# Revit family: Касетный компактный блок VRF системы
name_source: partatom
category: Mechanical Equipment
revit_build: Autodesk Revit 2016 (Build: 20150506_1715(x64)
units: mm (PartAtom-declared; Revit-internal decimal feet)

## family parameters
Cut with Voids When Loaded = No
Host = Face
Part Type = Normal
Room Calculation Point = No
Round Connector Dimension = Use Diameter
Shared = No

## types (5) — shared parameters
Default Elevation = 1219.2 mm  [stored 4 ft]
Артикул планка = 1022724
Вес = 20.00 kg
Вес декоративной планки = 2.40 kg
Высота = 270 mm  [stored 0.885827 ft]
Высота планки = 30 mm  [stored 0.0984252 ft]
Глубина = 570 mm  [stored 1.87008 ft]
Глубина планки = 650 mm  [stored 2.13255 ft]
Диаметр дренажного шлага = 25 mm  [stored 0.082021 ft]
Диаметр жидкостной трубы = 6.35 mm  [stored 0.0208333 ft]
Модель декоративной планки = ESVMCP-SF-600
Наименование = Касетный компактный блок VRF-системы
Наименование декоративной планки = Декоративная панель для кассетного компактного блока
Напор дренажной помпы, мм водяного столба = 650
Номинал предохранителя = 10 A
Производитель = Electrolux
Таблица модель = Модель
Таблица модель планка = Модель планка
Таблица наименование = Наименование
Таблица наименование планка = Наименование планка
Таблица напор дренажной помпы = Напор дренажной помпы
Таблица параметров = Таблица параметров
Таблица параметров планка = Таблица параметров планка
Таблица расход воздуха = Расход воздуха
Таблица тип хладагента = Тип хладагента
Таблица уровень звукового давления = Уровень звукового давления
Таблица электропитание = Электропитание
Фаза = 1
Частота сети = 50 Hz
Ширина = 570 mm  [stored 1.87008 ft]
Ширина планки = 650 mm  [stored 2.13255 ft]
Эл. питание(коннектор) = 220 V
Электропитание, (В) = 220

## per-type parameters (varying)
| type | Артикул | Диаметр газовой трубы | Максимальная потребляемая мощность | Расход воздуха, (м.куб/ч) | Теплопроизводительность | Уровень звукового давления, (Дб(А)) | Холодопроизводительность |
| ESVMC4/C-SF-22 | 1022680 | 12.7 mm  [stored 0.0416667 ft] | 0.12 kW | 570-540-384 | 2.80 kW | 32-30-28 | 2.20 kW |
| ESVMC4/C-SF-28 | 1022681 | 12.7 mm  [stored 0.0416667 ft] | 0.12 kW | 570-540-384 | 3.30 kW | 32-30-28 | 2.80 kW |
| ESVMC4/C-SF-36 | 1022682 | 12.7 mm  [stored 0.0416667 ft] | 0.12 kW | 570-540-384 | 4.20 kW | 32-30-28 | 3.60 kW |
| ESVMC4/C-SF-45 | 1022683 | 12.7 mm  [stored 0.0416667 ft] | 0.13 kW | 654-564-456 | 4.90 kW | 34-32-30 | 4.30 kW |
| ESVMC4/C-SF-50 | 1022684 | 15.88 mm  [stored 0.0520997 ft] | 0.17 kW | 792-690-588 | 5.60 kW | 35-33-31 | 5.00 kW |

note: column(s) folded — value = type name in every type: Модель

note: [stored X ft] marks values corroborated as IEEE doubles in the binary element streams (Revit-internal decimal feet)
